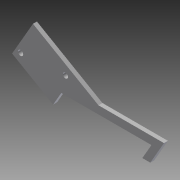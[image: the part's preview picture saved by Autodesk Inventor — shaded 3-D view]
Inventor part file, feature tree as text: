
AUTODESK INVENTOR PART (.ipt)
format: ipt  version: 2013 (Build 170138000, 138)  size: 97,792 bytes
history: native  units: in
note: dims shown in document units (in); Inventor stores cm internally (conversion verified against a paired STEP export)
features: extrude x1, sketch x1
ambient origin geometry x8: Origin, YZ Plane, XZ Plane, XY Plane, X Axis, Y Axis, Z Axis, Center Point
bodies: Solid1 (feature_tree)
feature tree (2):
  extrude  "Extrusion1"  Depth=5.3671in
  sketch  "Sketch1"  dims[d14=0.5in d39=5.12in d41=1.0in d42=0.5in d43=60.0deg d44=60.0deg d45=0.5in d51=5.3671in d54=5.3671in d55=0.5in d56=2.62in d57=1.319in d58=1.319in d59=2.992in d60=1.6077in d61=0.315in d63=0.3268in d64=0.315in d66=0.327in d67=0.25in d68=0.0in]
